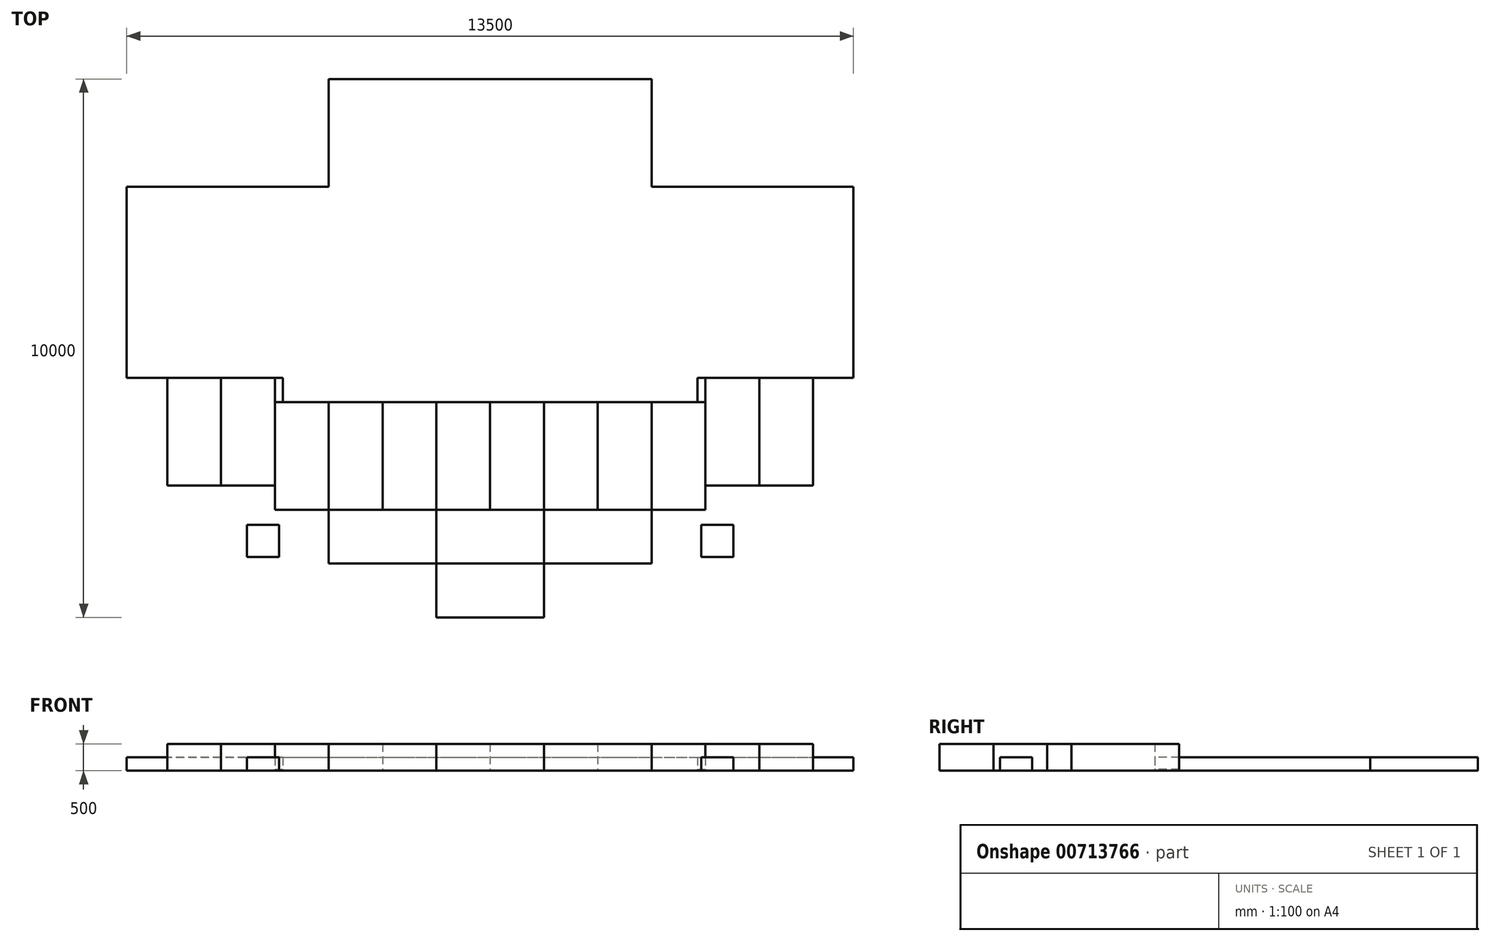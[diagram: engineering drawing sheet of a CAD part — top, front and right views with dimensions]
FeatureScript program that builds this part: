
annotation { "Feature Type Name" : "Feature", "Feature Type Description" : "" }
export const myFeature = defineFeature(function(context is Context, id is Id, definition is map)
    precondition{}
    {
        {
            var Q0;
            Q0=qCreatedBy(makeId("Top.planeOp"),FACE);
            var sketch = newSketch(context, id + "F0", { "sketchPlane" : qUnion([Q0])});
            skLineSegment(sketch, "E0.bottom", {"start": v(0, 0) * mm, "end": v(1000, 0) * mm});
            skLineSegment(sketch, "E0.top", {"start": v(0, 2000) * mm, "end": v(1000, 2000) * mm});
            skLineSegment(sketch, "E0.left", {"start": v(0, 0) * mm, "end": v(0, 2000) * mm});
            skLineSegment(sketch, "E0.right", {"start": v(1000, 0) * mm, "end": v(1000, 2000) * mm});
            skLineSegment(sketch, "E1", {"start": v(1000, 2000) * mm, "end": v(2000, 2000) * mm});
            skLineSegment(sketch, "E2", {"start": v(2000, 2000) * mm, "end": v(3000, 2000) * mm});
            skLineSegment(sketch, "E3", {"start": v(3000, 2000) * mm, "end": v(4000, 2000) * mm});
            skLineSegment(sketch, "E4", {"start": v(4000, 2000) * mm, "end": v(5000, 2000) * mm});
            skLineSegment(sketch, "E5", {"start": v(5000, 2000) * mm, "end": v(6000, 2000) * mm});
            skLineSegment(sketch, "E6", {"start": v(6000, 2000) * mm, "end": v(7000, 2000) * mm});
            skLineSegment(sketch, "E7", {"start": v(7000, 2000) * mm, "end": v(8000, 2000) * mm});
            skLineSegment(sketch, "E8", {"start": v(1000, 0) * mm, "end": v(2000, 0) * mm});
            skLineSegment(sketch, "E9", {"start": v(2000, 0) * mm, "end": v(3000, 0) * mm});
            skLineSegment(sketch, "E10", {"start": v(3000, 0) * mm, "end": v(4000, 0) * mm});
            skLineSegment(sketch, "E11", {"start": v(4000, 0) * mm, "end": v(5000, 0) * mm});
            skLineSegment(sketch, "E12", {"start": v(5000, 0) * mm, "end": v(6000, 0) * mm});
            skLineSegment(sketch, "E13", {"start": v(6000, 0) * mm, "end": v(7000, 0) * mm});
            skLineSegment(sketch, "E14", {"start": v(7000, 0) * mm, "end": v(8000, 0) * mm});
            skLineSegment(sketch, "E15", {"start": v(8000, 0) * mm, "end": v(8000, 2000) * mm});
            skLineSegment(sketch, "E16", {"start": v(2000, 2000) * mm, "end": v(2000, 0) * mm});
            skLineSegment(sketch, "E17", {"start": v(3000, 2000) * mm, "end": v(3000, 0) * mm});
            skLineSegment(sketch, "E18", {"start": v(4000, 2000) * mm, "end": v(4000, 0) * mm});
            skLineSegment(sketch, "E19", {"start": v(5000, 2000) * mm, "end": v(5000, 0) * mm});
            skLineSegment(sketch, "E20", {"start": v(6000, 2000) * mm, "end": v(6000, 0) * mm});
            skLineSegment(sketch, "E21", {"start": v(7000, 2000) * mm, "end": v(7000, 0) * mm});
            skLineSegment(sketch, "E22", {"start": v(8000, 2000) * mm, "end": v(8000, 2450) * mm});
            skLineSegment(sketch, "E23", {"start": v(8000, 2450) * mm, "end": v(9000, 2450) * mm});
            skLineSegment(sketch, "E24", {"start": v(9000, 2450) * mm, "end": v(9000, 450) * mm});
            skLineSegment(sketch, "E25", {"start": v(9000, 450) * mm, "end": v(8000, 450) * mm});
            skLineSegment(sketch, "E26", {"start": v(9000, 2450) * mm, "end": v(10000, 2450) * mm});
            skLineSegment(sketch, "E27", {"start": v(10000, 2450) * mm, "end": v(10000, 450) * mm});
            skLineSegment(sketch, "E28", {"start": v(10000, 450) * mm, "end": v(9000, 450) * mm});
            skLineSegment(sketch, "E29", {"start": v(0, 2450) * mm, "end": v(0, 2000) * mm});
            skLineSegment(sketch, "E30", {"start": v(-1000, 2450) * mm, "end": v(-1000, 450) * mm});
            skLineSegment(sketch, "E31", {"start": v(-1000, 450) * mm, "end": v(0, 450) * mm});
            skLineSegment(sketch, "E32", {"start": v(-1000, 450) * mm, "end": v(-2000, 450) * mm});
            skLineSegment(sketch, "E33", {"start": v(-2000, 450) * mm, "end": v(-2000, 2450) * mm});
            skLineSegment(sketch, "E34", {"start": v(-2000, 2450) * mm, "end": v(-1000, 2450) * mm});
            skLineSegment(sketch, "E35", {"start": v(0, 2450) * mm, "end": v(-1000, 2450) * mm});
            skLineSegment(sketch, "E36", {"start": v(3000, 0) * mm, "end": v(3000, -1000) * mm});
            skLineSegment(sketch, "E37", {"start": v(3000, -1000) * mm, "end": v(5000, -1000) * mm});
            skLineSegment(sketch, "E38", {"start": v(5000, -1000) * mm, "end": v(5000, 0) * mm});
            skLineSegment(sketch, "E39", {"start": v(5000, -1000) * mm, "end": v(7000, -1000) * mm});
            skLineSegment(sketch, "E40", {"start": v(7000, -1000) * mm, "end": v(7000, 0) * mm});
            skLineSegment(sketch, "E41", {"start": v(3000, -1000) * mm, "end": v(1000, -1000) * mm});
            skLineSegment(sketch, "E42", {"start": v(1000, -1000) * mm, "end": v(1000, 0) * mm});
            skLineSegment(sketch, "E43", {"start": v(3000, -1000) * mm, "end": v(3000, -2000) * mm});
            skLineSegment(sketch, "E44", {"start": v(3000, -2000) * mm, "end": v(5000, -2000) * mm});
            skLineSegment(sketch, "E45", {"start": v(5000, -2000) * mm, "end": v(5000, -1000) * mm});
            skLineSegment(sketch, "E46", {"start": v(8000, 2450) * mm, "end": v(7850, 2450) * mm});
            skLineSegment(sketch, "E47", {"start": v(7850, 2450) * mm, "end": v(7850, 2000) * mm});
            skLineSegment(sketch, "E48", {"start": v(0, 2450) * mm, "end": v(150, 2450) * mm});
            skLineSegment(sketch, "E49", {"start": v(150, 2450) * mm, "end": v(150, 2000) * mm});
            skLineSegment(sketch, "E50", {"start": v(-2000, 2450) * mm, "end": v(-2750, 2450) * mm});
            skLineSegment(sketch, "E51", {"start": v(10750, 2450) * mm, "end": v(10000, 2450) * mm});
            skLineSegment(sketch, "E52.bottom", {"start": v(-520, -280) * mm, "end": v(80, -280) * mm});
            skLineSegment(sketch, "E52.top", {"start": v(-520, -880) * mm, "end": v(80, -880) * mm});
            skLineSegment(sketch, "E52.left", {"start": v(-520, -280) * mm, "end": v(-520, -880) * mm});
            skLineSegment(sketch, "E52.right", {"start": v(80, -280) * mm, "end": v(80, -880) * mm});
            skLineSegment(sketch, "E53.bottom", {"start": v(7920, -280) * mm, "end": v(8520, -280) * mm});
            skLineSegment(sketch, "E53.top", {"start": v(7920, -880) * mm, "end": v(8520, -880) * mm});
            skLineSegment(sketch, "E53.left", {"start": v(7920, -280) * mm, "end": v(7920, -880) * mm});
            skLineSegment(sketch, "E53.right", {"start": v(8520, -280) * mm, "end": v(8520, -880) * mm});
            skLineSegment(sketch, "E54", {"start": v(-2750, 2450) * mm, "end": v(-2750, 6000) * mm});
            skLineSegment(sketch, "E55", {"start": v(-2750, 6000) * mm, "end": v(1000, 6000) * mm});
            skLineSegment(sketch, "E56", {"start": v(1000, 6000) * mm, "end": v(1000, 8000) * mm});
            skLineSegment(sketch, "E57", {"start": v(1000, 8000) * mm, "end": v(7000, 8000) * mm});
            skLineSegment(sketch, "E58", {"start": v(7000, 8000) * mm, "end": v(7000, 6000) * mm});
            skLineSegment(sketch, "E59", {"start": v(7000, 6000) * mm, "end": v(10750, 6000) * mm});
            skLineSegment(sketch, "E60", {"start": v(10750, 6000) * mm, "end": v(10750, 2450) * mm});
            skSolve(sketch);
        }
        {
            var Q0;
            Q0=makeQuery(id+"F0.imprint","IMPRINT",FACE,{"disambiguationData":[TD([[makeQuery(id+"F0.imprint","IMPRINT",EDGE,{"derivedFrom":sQuery(id+"F0.wireOp",EDGE,"E30")}),-1.0]])]});
            extrude(context, id + "F1", {"entities" : qUnion([Q0]), "depth" : 500 * mm, "offsetDistance" : 25 * mm});
        }
        {
            var Q0;
            {var subQ1=sQuery(id+"F0.wireOp",EDGE,"E0.bottom");Q0=makeQuery(id+"F0.imprint","IMPRINT",FACE,{"disambiguationData":[TD([[makeQuery(id+"F0.imprint","IMPRINT",EDGE,{"derivedFrom":subQ1}),1.0]])]});}
            var Q1;
            Q1=makeQuery(id+"F0.imprint","IMPRINT",FACE,{"disambiguationData":[TD([[makeQuery(id+"F0.imprint","IMPRINT",EDGE,{"derivedFrom":sQuery(id+"F0.wireOp",EDGE,"E2")}),-1.0]])]});
            var Q2;
            Q2=makeQuery(id+"F0.imprint","IMPRINT",FACE,{"disambiguationData":[TD([[makeQuery(id+"F0.imprint","IMPRINT",EDGE,{"derivedFrom":sQuery(id+"F0.wireOp",EDGE,"E4")}),-1.0]])]});
            var Q3;
            Q3=makeQuery(id+"F0.imprint","IMPRINT",FACE,{"disambiguationData":[TD([[makeQuery(id+"F0.imprint","IMPRINT",EDGE,{"derivedFrom":sQuery(id+"F0.wireOp",EDGE,"E6")}),-1.0]])]});
            var Q4;
            {var subQ0=sQuery(id+"F0.wireOp",EDGE,"E22");Q4=makeQuery(id+"F0.imprint","IMPRINT",FACE,{"disambiguationData":[TD([[makeQuery(id+"F0.imprint","IMPRINT",EDGE,{"derivedFrom":subQ0}),-1.0]])]});}
            extrude(context, id + "F2", {"entities" : qUnion([Q0, Q1, Q2, Q3, Q4]), "depth" : 500 * mm, "offsetDistance" : 25 * mm});
        }
        {
            var Q0;
            {var subQ1=sQuery(id+"F0.wireOp",EDGE,"E29");Q0=makeQuery(id+"F0.imprint","IMPRINT",FACE,{"disambiguationData":[TD([[makeQuery(id+"F0.imprint","IMPRINT",EDGE,{"derivedFrom":subQ1}),-1.0]])]});}
            var Q1;
            Q1=makeQuery(id+"F0.imprint","IMPRINT",FACE,{"disambiguationData":[TD([[makeQuery(id+"F0.imprint","IMPRINT",EDGE,{"derivedFrom":sQuery(id+"F0.wireOp",EDGE,"E0.right")}),-1.0]])]});
            var Q2;
            Q2=makeQuery(id+"F0.imprint","IMPRINT",FACE,{"disambiguationData":[TD([[makeQuery(id+"F0.imprint","IMPRINT",EDGE,{"derivedFrom":sQuery(id+"F0.wireOp",EDGE,"E3")}),-1.0]])]});
            var Q3;
            Q3=makeQuery(id+"F0.imprint","IMPRINT",FACE,{"disambiguationData":[TD([[makeQuery(id+"F0.imprint","IMPRINT",EDGE,{"derivedFrom":sQuery(id+"F0.wireOp",EDGE,"E5")}),-1.0]])]});
            var Q4;
            {var subQ1=sQuery(id+"F0.wireOp",EDGE,"E14");Q4=makeQuery(id+"F0.imprint","IMPRINT",FACE,{"disambiguationData":[TD([[makeQuery(id+"F0.imprint","IMPRINT",EDGE,{"derivedFrom":subQ1}),1.0]])]});}
            var Q5;
            Q5=makeQuery(id+"F0.imprint","IMPRINT",FACE,{"disambiguationData":[TD([[makeQuery(id+"F0.imprint","IMPRINT",EDGE,{"derivedFrom":sQuery(id+"F0.wireOp",EDGE,"E24")}),1.0]])]});
            extrude(context, id + "F3", {"entities" : qUnion([Q0, Q1, Q2, Q3, Q4, Q5]), "depth" : 500 * mm, "offsetDistance" : 25 * mm});
        }
        {
            var Q0;
            Q0=makeQuery(id+"F0.imprint","IMPRINT",FACE,{"disambiguationData":[TD([[makeQuery(id+"F0.imprint","IMPRINT",EDGE,{"derivedFrom":sQuery(id+"F0.wireOp",EDGE,"E8")}),-1.0]])]});
            var Q1;
            Q1=makeQuery(id+"F0.imprint","IMPRINT",FACE,{"disambiguationData":[TD([[makeQuery(id+"F0.imprint","IMPRINT",EDGE,{"derivedFrom":sQuery(id+"F0.wireOp",EDGE,"E37")}),-1.0]])]});
            var Q2;
            Q2=makeQuery(id+"F0.imprint","IMPRINT",FACE,{"disambiguationData":[TD([[makeQuery(id+"F0.imprint","IMPRINT",EDGE,{"derivedFrom":sQuery(id+"F0.wireOp",EDGE,"E12")}),-1.0]])]});
            extrude(context, id + "F4", {"entities" : qUnion([Q0, Q1, Q2]), "depth" : 500 * mm, "offsetDistance" : 25 * mm});
        }
        {
            var Q0;
            {var subQ0=sQuery(id+"F0.wireOp",EDGE,"E29");Q0=makeQuery(id+"F0.imprint","IMPRINT",FACE,{"disambiguationData":[TD([[makeQuery(id+"F0.imprint","IMPRINT",EDGE,{"derivedFrom":subQ0}),1.0]])]});}
            var Q1;
            {var subQ0=sQuery(id+"F0.wireOp",EDGE,"E22");Q1=makeQuery(id+"F0.imprint","IMPRINT",FACE,{"disambiguationData":[TD([[makeQuery(id+"F0.imprint","IMPRINT",EDGE,{"derivedFrom":subQ0}),1.0]])]});}
            extrude(context, id + "F5", {"entities" : qUnion([Q0, Q1]), "depth" : 25 * mm, "offsetDistance" : 25 * mm});
        }
        {
            var Q0;
            Q0=makeQuery(id+"F0.imprint","IMPRINT",FACE,{"disambiguationData":[TD([[makeQuery(id+"F0.imprint","IMPRINT",EDGE,{"derivedFrom":sQuery(id+"F0.wireOp",EDGE,"E10")}),-1.0]])]});
            extrude(context, id + "F6", {"entities" : qUnion([Q0]), "depth" : 500 * mm, "offsetDistance" : 25 * mm});
        }
        {
            var Q0;
            {var subQ4=sQuery(id+"F0.wireOp",EDGE,"E1");Q0=makeQuery(id+"F0.imprint","IMPRINT",FACE,{"disambiguationData":[TD([[makeQuery(id+"F0.imprint","IMPRINT",EDGE,{"derivedFrom":subQ4}),1.0]])]});}
            var Q1;
            Q1=makeQuery(id+"F0.imprint","IMPRINT",FACE,{"disambiguationData":[TD([[makeQuery(id+"F0.imprint","IMPRINT",EDGE,{"derivedFrom":sQuery(id+"F0.wireOp",EDGE,"E52.bottom")}),-1.0]])]});
            var Q2;
            Q2=makeQuery(id+"F0.imprint","IMPRINT",FACE,{"disambiguationData":[TD([[makeQuery(id+"F0.imprint","IMPRINT",EDGE,{"derivedFrom":sQuery(id+"F0.wireOp",EDGE,"E53.bottom")}),-1.0]])]});
            extrude(context, id + "F7", {"entities" : qUnion([Q0, Q1, Q2]), "depth" : 250 * mm, "offsetDistance" : 25 * mm});
        }
    });
